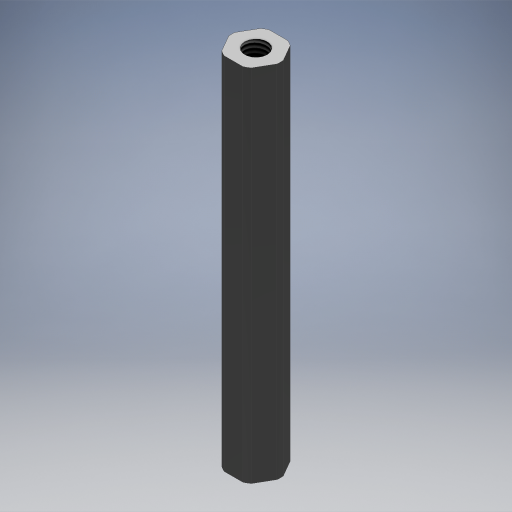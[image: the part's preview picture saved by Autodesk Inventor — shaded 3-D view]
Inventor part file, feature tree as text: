
AUTODESK INVENTOR PART (.ipt)
format: ipt  version: 2024.2 (Build 282272000, 272)  size: 461,312 bytes
history: native  units: in
note: dims shown in document units (in); Inventor stores cm internally (conversion verified against a paired STEP export)
features: extrude x32, other x4, hole x2
ambient origin geometry x8: Origin, YZ Plane, XZ Plane, XY Plane, X Axis, Y Axis, Z Axis, Center Point
bodies: Solid3 (feature_tree)
feature tree (38):
  extrude  "BaseProfile625Round"  Depth=0.5in
  extrude  "BaseProfileRoundTube"  Depth=0.5413in
  extrude  "BaseProfile500Hex"  Depth=0.5in
  extrude  "BaseProfile500Thunderhex"  Depth=0.375in
  extrude  "BaseProfile500Round"  Depth=0.4035in
  extrude  "BaseProfile375Hex"  Depth=0.75in
  extrude  "BaseProfile375Thunderhex"  Depth=0.468in
  extrude  "BaseProfile375Round"  Depth=0.201in
  extrude  "TopShaftProfile1Hex500"  Depth=0.159in
  extrude  "TopShaftProfile1ThunderHex500"  Depth=0.25in
  extrude  "TopShaftProfile1Round500"  Depth=36.0in TaperAngle=0.0deg
  extrude  "TopShaftProfile1Hex375"  Depth=4.0in TaperAngle=0.0deg
  extrude  "TopShaftProfile1ThunderHex375"  Depth=36.0in TaperAngle=0.0deg
  extrude  "TopShaftProfile1Round375"  Depth=36.0in TaperAngle=0.0deg
  extrude  "TopShaftProfile2ThunderHex500"  Depth=36.0in TaperAngle=0.0deg
  extrude  "TopShaftProfile2Round500"  Depth=36.0in TaperAngle=0.0deg
  extrude  "TopShaftProfile2Hex375"  Depth=36.0in TaperAngle=0.0deg
  extrude  "TopShaftProfile2ThunderHex375"  Depth=36.0in TaperAngle=0.0deg
  extrude  "TopShaftProfile2Round375"  Depth=36.0in TaperAngle=0.0deg
  other  "TopRetentionGroove&BearingRound"
  hole  "TopShaftTappedHole"  [1 undecoded]
  other  "TopShaftThread"
  extrude  "BottomShaftProfile1Hex500"  TaperAngle=0.0deg  [1 undecoded]
  extrude  "BottomShaftProfile1ThunderHex500"  TaperAngle=0.0deg  [1 undecoded]
  extrude  "BottomShaftProfile1Round500"  TaperAngle=0.0deg  [1 undecoded]
  extrude  "BottomShaftProfile1Hex375"  TaperAngle=0.0deg  [1 undecoded]
  extrude  "BottomShaftProfile1ThunderHex375"  TaperAngle=0.0deg  [1 undecoded]
  extrude  "BottomShaftProfile2ThunderHex500"  TaperAngle=0.0deg  [1 undecoded]
  extrude  "BottomShaftProfile1Round375"  TaperAngle=0.0deg  [1 undecoded]
  extrude  "BottomShaftProfile2Round500"  TaperAngle=0.0deg  [1 undecoded]
  extrude  "BottomShaftProfile2Hex375"  TaperAngle=0.0deg  [1 undecoded]
  extrude  "BottomShaftProfile2ThunderHex375"  TaperAngle=0.0deg  [1 undecoded]
  extrude  "BottomShaftProfile2Round375"  TaperAngle=0.0deg  [1 undecoded]
  hole  "BottomShaftTappedHole"  [1 undecoded]
  other  "BottomShaftThread"
  other  "BottomRetentionGroove&BearingRound"
  extrude  "BaseProfile375ThunderhexHole"  TaperAngle=0.0deg  [1 undecoded]
  extrude  "BaseProfile500ThunderhexHole"  TaperAngle=0.0deg  [1 undecoded]
note: 15 required parameter values undecoded (feature->parameter linkage not recoverable at this tier; creation-order binding heuristic only, values carry confidence <= 0.55)
